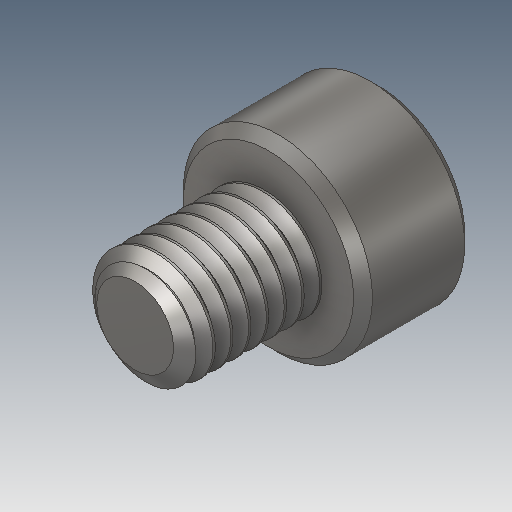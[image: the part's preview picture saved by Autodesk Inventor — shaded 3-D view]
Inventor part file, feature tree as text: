
AUTODESK INVENTOR PART (.ipt)
format: ipt  version: 2017 (Build 210142000, 142)  size: 684,032 bytes
history: native  units: mm
features: chamfer x1
ambient origin geometry x8: Origin, YZ Plane, XZ Plane, XY Plane, X Axis, Y Axis, Z Axis, Center Point
bodies: Solid1 (feature_tree)
feature tree (1):
  chamfer  "Chamfer1"  [1 undecoded]
note: 1 required parameter value undecoded (feature->parameter linkage not recoverable at this tier; creation-order binding heuristic only, values carry confidence <= 0.55)
